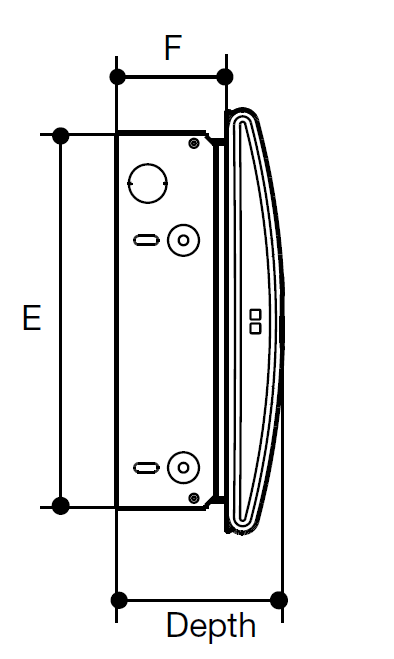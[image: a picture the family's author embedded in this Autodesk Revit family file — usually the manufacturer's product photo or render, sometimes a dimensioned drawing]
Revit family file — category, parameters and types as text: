
# Revit family: Hager-SM_Design_50-Configurable_High_Integrity-UK-en
name_source: partatom
category: Electrical Equipment
units: mm (PartAtom-declared; Revit-internal decimal feet)

## family parameters
Cut with Voids When Loaded = No
Host = Face
Panel Configuration = Two Columns, Circuits Across
Part Type = Panelboard
Room Calculation Point = No
Round Connector Dimension = Use Diameter
Shared = No

## types (4) — shared parameters
Classification.Uniclass.Pr.Description = Control circuit device enclosures
Classification.Uniclass.Pr.Number = Pr_80_77_28_16
Default Elevation = 11 mm  [stored 0.0360892 ft]
EF000007 - Colour = EV000202 - White
EF000040 - Height = 284 mm  [stored 0.931759 ft]
EF000049 - Depth = 105 mm  [stored 0.344488 ft]
EF000116 - RAL-number = 9010
EF000118 - With mounting plate = No
EF000218 - Built-in depth = 72 mm  [stored 0.23622 ft]
EF000266 - Number of rows = 1
EF000332 - Built-in height = 252 mm  [stored 0.826772 ft]
EF000339 - Type of cover = EV001012 - Cover
EF001062 - EMC-version = No
EF001088 - Extension possible = Yes
EF001134 - DIN-rail = No
EF001596 - Material housing = EV000179 - Steel
EF004462 - Type of closure = EV000154 - Other
EF005474 - Degree of protection (IP) = EV009848 - IP2XC
EF006244 - Transparent cover/door = No
EF006306 - With lock = No
EF009212 - Cover model = EV000116 - Closed
EF015941 - Signal passing door = No
Ground Bus = No
HG000002 - With door or cover = Yes
HG000003 - Range = Surface Mounting Consumer Units
HG000005 - Thickness = 3 mm  [stored 0.00984252 ft]
HG000017 - Distance between poles = 18 mm  [stored 0.0590551 ft]
Manufacturer = Hager
Neutral Bus = No
Type Comments = Surface Mounting Consumer Units
zero-valued in all types: EF001131 - Internal depth, EF002950 - Width in number of modular spacings

## per-type parameters (varying)
| type | EF000003 - Mounting method | EF000008 - Width | EF000846 - Built-in width | EF015776 - Earthing terminal block | EF015777 - Neutral terminal block | HG000004 - Manufacturer reference | HG000006 - Flush mounted | Model |
| Recessed mounted P2XC W467 H284 D105  Modular spacings - VSR910CUSPD | EV000383 - Flush mounted (plaster) | 467 mm  [stored 1.53215 ft] | 406 mm  [stored 1.33202 ft] | Yes | Yes | VSR910CUSPD | Yes | VSR910CUSPD |
| Surface mounted P2XC W431 H284 D105  Modular spacings - VSR910CU | EV000384 - Surface mounted (plaster) | 431 mm  [stored 1.41404 ft] | 370 mm  [stored 1.21391 ft] | No | No | VSR910CU | No | VSR910CU |
| Surface mounted P2XC W467 H284 D105  Modular spacings - VSR912CU | EV000384 - Surface mounted (plaster) | 467 mm  [stored 1.53215 ft] | 406 mm  [stored 1.33202 ft] | No | Yes | VSR912CU | No | VSR912CU |
| Surface mounted P2XC W539 H284 D105  Modular spacings - VSR916CU | EV000384 - Surface mounted (plaster) | 539 mm  [stored 1.76837 ft] | 478 mm  [stored 1.56824 ft] | Yes | Yes | VSR916CU | No | VSR916CU |

note: [stored X ft] marks values corroborated as IEEE doubles in the binary element streams (Revit-internal decimal feet)

## geometry (parser evidence)
native form markers: Blend x4, Revolve x2, Sweep x13
no freeform markers — native parametric forms only
